FCSTD DOCUMENT  (FreeCAD 0.20R29410 (Git))
Label: Chamber0
License: All rights reserved
LicenseURL: http://en.wikipedia.org/wiki/All_rights_reserved
objects: Sketcher::SketchObject×3, PartDesign::Body×1
note: 4 computed .brp shape members not serialized (recipe doc carries the construction recipe); baked Part::Feature solids carry a one-line shape summary decoded from their .brp

FEATURE [PartDesign::Body] Body
  Origin = -> Origin
FEATURE [Sketcher::SketchObject] Sketch001
  FullyConstrained = false
  sketch-geometry (28):
    g0: ArcOfCircle CenterX=0 CenterY=0 CenterZ=0 NormalX=0 NormalY=0 NormalZ=1 AngleXU=0 Radius=100 StartAngle=0.785398 EndAngle=2.35619
    g1: Circle CenterX=0 CenterY=116 CenterZ=0 NormalX=0 NormalY=0 NormalZ=1 AngleXU=0 Radius=6
    g2: ArcOfCircle CenterX=0 CenterY=0 CenterZ=0 NormalX=0 NormalY=0 NormalZ=1 AngleXU=0 Radius=120 StartAngle=1.73306 EndAngle=2.35619
    g3: GeomPoint X=0 Y=100 Z=0
    g4: GeomPoint X=0 Y=120 Z=0
    g5: ArcOfCircle CenterX=0 CenterY=116 CenterZ=0 NormalX=0 NormalY=0 NormalZ=1 AngleXU=0 Radius=16 StartAngle=4.71239 EndAngle=4.71239
    g6: GeomPoint X=0 Y=132 Z=0
    g7: ArcOfCircle CenterX=0 CenterY=116 CenterZ=0 NormalX=0 NormalY=0 NormalZ=1 AngleXU=0 Radius=16 StartAngle=0.329187 EndAngle=2.75254
    g8: ArcOfCircle CenterX=-20.3559 CenterY=124.345 CenterZ=0 NormalX=0 NormalY=0 NormalZ=1 AngleXU=0 Radius=6 StartAngle=4.87466 EndAngle=5.89413
    g9: ArcOfCircle CenterX=0 CenterY=116 CenterZ=0 NormalX=0 NormalY=0 NormalZ=1 AngleXU=0 Radius=16 StartAngle=0.329187 EndAngle=2.75254
    g10: ArcOfCircle CenterX=18.7837 CenterY=122.417 CenterZ=0 NormalX=0 NormalY=0 NormalZ=1 AngleXU=0 Radius=3.84956 StartAngle=3.47078 EndAngle=4.56014
    g11: ArcOfCircle CenterX=0 CenterY=0 CenterZ=0 NormalX=0 NormalY=0 NormalZ=1 AngleXU=0 Radius=120 StartAngle=0.785398 EndAngle=1.41854
    g12: ArcOfCircle CenterX=0 CenterY=116 CenterZ=0 NormalX=0 NormalY=0 NormalZ=1 AngleXU=0 Radius=16 StartAngle=4.71239 EndAngle=4.71239
    g13: ArcOfCircle CenterX=0 CenterY=116 CenterZ=0 NormalX=0 NormalY=0 NormalZ=1 AngleXU=0 Radius=16 StartAngle=0.329187 EndAngle=2.75254
    g14: ArcOfCircle CenterX=0 CenterY=0 CenterZ=0 NormalX=0 NormalY=0 NormalZ=1 AngleXU=0 Radius=100 StartAngle=3.92699 EndAngle=5.49779
    g15: Circle CenterX=0 CenterY=-116 CenterZ=0 NormalX=0 NormalY=0 NormalZ=1 AngleXU=0 Radius=6
    g16: ArcOfCircle CenterX=0 CenterY=0 CenterZ=0 NormalX=0 NormalY=0 NormalZ=1 AngleXU=0 Radius=120 StartAngle=3.92699 EndAngle=4.55012
    g17: GeomPoint X=0 Y=-100 Z=0
    g18: GeomPoint X=0 Y=-120 Z=0
    g19: ArcOfCircle CenterX=0 CenterY=-116 CenterZ=0 NormalX=0 NormalY=0 NormalZ=1 AngleXU=0 Radius=16 StartAngle=1.5708 EndAngle=1.5708
    g20: GeomPoint X=0 Y=-132 Z=0
    g21: ArcOfCircle CenterX=0 CenterY=-116 CenterZ=0 NormalX=0 NormalY=0 NormalZ=1 AngleXU=0 Radius=16 StartAngle=3.53064 EndAngle=5.954
    g22: ArcOfCircle CenterX=-20.3559 CenterY=-124.345 CenterZ=0 NormalX=0 NormalY=0 NormalZ=1 AngleXU=0 Radius=6 StartAngle=0.389051 EndAngle=1.40853
    g23: ArcOfCircle CenterX=0 CenterY=-116 CenterZ=0 NormalX=0 NormalY=0 NormalZ=1 AngleXU=0 Radius=16 StartAngle=3.53064 EndAngle=5.954
    g24: ArcOfCircle CenterX=18.7837 CenterY=-122.417 CenterZ=0 NormalX=0 NormalY=0 NormalZ=1 AngleXU=0 Radius=3.84956 StartAngle=1.72305 EndAngle=2.81241
    g25: ArcOfCircle CenterX=0 CenterY=0 CenterZ=0 NormalX=0 NormalY=0 NormalZ=1 AngleXU=0 Radius=120 StartAngle=4.86464 EndAngle=5.49779
    g26: ArcOfCircle CenterX=0 CenterY=-116 CenterZ=0 NormalX=0 NormalY=0 NormalZ=1 AngleXU=0 Radius=16 StartAngle=1.5708 EndAngle=1.5708
    g27: ArcOfCircle CenterX=0 CenterY=-116 CenterZ=0 NormalX=0 NormalY=0 NormalZ=1 AngleXU=0 Radius=16 StartAngle=3.53064 EndAngle=5.954
  constraints (71):
    c: Coincident(g0,g-1)
    c: Radius(g0) = 100
    c: Radius(g1) = 6  'Main Screw Radius 0'
    c: Vertical(g1,g0)
    c: Coincident(g2,g0)
    c: PointOnObject(g3,g0)
    c: Vertical(g3,g0)
    c: PointOnObject(g4,g2)
    c: Vertical(g0,g4)
    c: Distance(g4,g3) = 20
    c: Coincident(g5,g1)
    c: Radius(g5) = 16  'Main Clamp Outer'
    c: PointOnObject(g6,g5)
    c: Vertical(g6,g1)
    c: Distance(g1,g3) = 16
    c: PointOnObject(g5,g0)
    c: Equal(g5,g7)
    c: Coincident(g5,g7)
    c: Tangent(g2,g8) = 1.5708
    c: Tangent(g7,g8) = 1.5708
    c: Radius(g8) = 6
    c: PointOnObject(g9,g8)
    c: Equal(g5,g9)
    c: PointOnObject(g12,g0)
    c: Coincident(g5,g9)
    c: Tangent(g7,g10) = 1.5708
    c: Coincident(g11,g10) = 1.5708
    c: PointOnObject(g9,g10)
    c: Equal(g2,g11)
    c: Coincident(g2,g11)
    c: Equal(g5,g12)
    c: PointOnObject(g13,g8)
    c: PointOnObject(g12,g0)
    c: Coincident(g5,g12)
    c: Equal(g5,g13)
    c: PointOnObject(g5,g0)
    c: PointOnObject(g13,g10)
    c: Coincident(g5,g13)
    c: Radius(g14) = 100
    c: Radius(g15) = 6  'Main Screw Radius 0'
    c: Coincident(g16,g14)
    c: PointOnObject(g17,g14)
    c: PointOnObject(g18,g16)
    c: Distance(g18,g17) = 20
    c: Coincident(g19,g15)
    c: Radius(g19) = 16  'Main Clamp Outer'
    c: PointOnObject(g20,g19)
    c: Distance(g15,g17) = 16
    c: PointOnObject(g19,g14)
    c: Equal(g19,g21)
    c: Coincident(g19,g21)
    c: Tangent(g16,g22) = 1.5708
    c: Tangent(g21,g22) = 1.5708
    c: Radius(g22) = 6
    c: PointOnObject(g23,g22)
    c: Equal(g19,g23)
    c: PointOnObject(g26,g14)
    c: Coincident(g19,g23)
    c: Tangent(g21,g24) = 1.5708
    c: Coincident(g25,g24) = 1.5708
    c: PointOnObject(g23,g24)
    c: Equal(g16,g25)
    c: Coincident(g16,g25)
    c: Equal(g19,g26)
    c: PointOnObject(g27,g22)
    c: PointOnObject(g26,g14)
    c: Coincident(g19,g26)
    c: Equal(g19,g27)
    c: PointOnObject(g19,g14)
    c: PointOnObject(g27,g24)
    c: Coincident(g19,g27)
FEATURE [Sketcher::SketchObject] Sketch002
  FullyConstrained = false
  Placement = pos=(0,0,0) rot=(0,0,1;1.5708rad)
  sketch-geometry (28):
    g0: ArcOfCircle CenterX=0 CenterY=0 CenterZ=0 NormalX=0 NormalY=0 NormalZ=1 AngleXU=0 Radius=100 StartAngle=0.785398 EndAngle=2.35619
    g1: Circle CenterX=0 CenterY=116 CenterZ=0 NormalX=0 NormalY=0 NormalZ=1 AngleXU=0 Radius=6
    g2: ArcOfCircle CenterX=0 CenterY=0 CenterZ=0 NormalX=0 NormalY=0 NormalZ=1 AngleXU=0 Radius=120 StartAngle=1.73306 EndAngle=2.35619
    g3: GeomPoint X=0 Y=100 Z=0
    g4: GeomPoint X=0 Y=120 Z=0
    g5: ArcOfCircle CenterX=0 CenterY=116 CenterZ=0 NormalX=0 NormalY=0 NormalZ=1 AngleXU=0 Radius=16 StartAngle=4.71239 EndAngle=4.71239
    g6: GeomPoint X=0 Y=132 Z=0
    g7: ArcOfCircle CenterX=0 CenterY=116 CenterZ=0 NormalX=0 NormalY=0 NormalZ=1 AngleXU=0 Radius=16 StartAngle=0.329187 EndAngle=2.75254
    g8: ArcOfCircle CenterX=-20.3559 CenterY=124.345 CenterZ=0 NormalX=0 NormalY=0 NormalZ=1 AngleXU=0 Radius=6 StartAngle=4.87466 EndAngle=5.89413
    g9: ArcOfCircle CenterX=0 CenterY=116 CenterZ=0 NormalX=0 NormalY=0 NormalZ=1 AngleXU=0 Radius=16 StartAngle=0.329187 EndAngle=2.75254
    g10: ArcOfCircle CenterX=18.7837 CenterY=122.417 CenterZ=0 NormalX=0 NormalY=0 NormalZ=1 AngleXU=0 Radius=3.84956 StartAngle=3.47078 EndAngle=4.56014
    g11: ArcOfCircle CenterX=0 CenterY=0 CenterZ=0 NormalX=0 NormalY=0 NormalZ=1 AngleXU=0 Radius=120 StartAngle=0.785398 EndAngle=1.41854
    g12: ArcOfCircle CenterX=0 CenterY=116 CenterZ=0 NormalX=0 NormalY=0 NormalZ=1 AngleXU=0 Radius=16 StartAngle=4.71239 EndAngle=4.71239
    g13: ArcOfCircle CenterX=0 CenterY=116 CenterZ=0 NormalX=0 NormalY=0 NormalZ=1 AngleXU=0 Radius=16 StartAngle=0.329187 EndAngle=2.75254
    g14: ArcOfCircle CenterX=0 CenterY=0 CenterZ=0 NormalX=0 NormalY=0 NormalZ=1 AngleXU=0 Radius=100 StartAngle=3.92699 EndAngle=5.49779
    g15: Circle CenterX=0 CenterY=-116 CenterZ=0 NormalX=0 NormalY=0 NormalZ=1 AngleXU=0 Radius=6
    g16: ArcOfCircle CenterX=0 CenterY=0 CenterZ=0 NormalX=0 NormalY=0 NormalZ=1 AngleXU=0 Radius=120 StartAngle=3.92699 EndAngle=4.55012
    g17: GeomPoint X=0 Y=-100 Z=0
    g18: GeomPoint X=0 Y=-120 Z=0
    g19: ArcOfCircle CenterX=0 CenterY=-116 CenterZ=0 NormalX=0 NormalY=0 NormalZ=1 AngleXU=0 Radius=16 StartAngle=1.5708 EndAngle=1.5708
    g20: GeomPoint X=0 Y=-132 Z=0
    g21: ArcOfCircle CenterX=0 CenterY=-116 CenterZ=0 NormalX=0 NormalY=0 NormalZ=1 AngleXU=0 Radius=16 StartAngle=3.53064 EndAngle=5.954
    g22: ArcOfCircle CenterX=-20.3559 CenterY=-124.345 CenterZ=0 NormalX=0 NormalY=0 NormalZ=1 AngleXU=0 Radius=6 StartAngle=0.389051 EndAngle=1.40853
    g23: ArcOfCircle CenterX=0 CenterY=-116 CenterZ=0 NormalX=0 NormalY=0 NormalZ=1 AngleXU=0 Radius=16 StartAngle=3.53064 EndAngle=5.954
    g24: ArcOfCircle CenterX=18.7837 CenterY=-122.417 CenterZ=0 NormalX=0 NormalY=0 NormalZ=1 AngleXU=0 Radius=3.84956 StartAngle=1.72305 EndAngle=2.81241
    g25: ArcOfCircle CenterX=0 CenterY=0 CenterZ=0 NormalX=0 NormalY=0 NormalZ=1 AngleXU=0 Radius=120 StartAngle=4.86464 EndAngle=5.49779
    g26: ArcOfCircle CenterX=0 CenterY=-116 CenterZ=0 NormalX=0 NormalY=0 NormalZ=1 AngleXU=0 Radius=16 StartAngle=1.5708 EndAngle=1.5708
    g27: ArcOfCircle CenterX=0 CenterY=-116 CenterZ=0 NormalX=0 NormalY=0 NormalZ=1 AngleXU=0 Radius=16 StartAngle=3.53064 EndAngle=5.954
  constraints (71):
    c: Coincident(g0,g-1)
    c: Radius(g0) = 100
    c: Radius(g1) = 6  'Main Screw Radius 0'
    c: Vertical(g1,g0)
    c: Coincident(g2,g0)
    c: PointOnObject(g3,g0)
    c: Vertical(g3,g0)
    c: PointOnObject(g4,g2)
    c: Vertical(g0,g4)
    c: Distance(g4,g3) = 20
    c: Coincident(g5,g1)
    c: Radius(g5) = 16  'Main Clamp Outer'
    c: PointOnObject(g6,g5)
    c: Vertical(g6,g1)
    c: Distance(g1,g3) = 16
    c: PointOnObject(g5,g0)
    c: Equal(g5,g7)
    c: Coincident(g5,g7)
    c: Tangent(g2,g8) = 1.5708
    c: Tangent(g7,g8) = 1.5708
    c: Radius(g8) = 6
    c: PointOnObject(g9,g8)
    c: Equal(g5,g9)
    c: PointOnObject(g12,g0)
    c: Coincident(g5,g9)
    c: Tangent(g7,g10) = 1.5708
    c: Coincident(g11,g10) = 1.5708
    c: PointOnObject(g9,g10)
    c: Equal(g2,g11)
    c: Coincident(g2,g11)
    c: Equal(g5,g12)
    c: PointOnObject(g13,g8)
    c: PointOnObject(g12,g0)
    c: Coincident(g5,g12)
    c: Equal(g5,g13)
    c: PointOnObject(g5,g0)
    c: PointOnObject(g13,g10)
    c: Coincident(g5,g13)
    c: Radius(g14) = 100
    c: Radius(g15) = 6  'Main Screw Radius 0'
    c: Coincident(g16,g14)
    c: PointOnObject(g17,g14)
    c: PointOnObject(g18,g16)
    c: Distance(g18,g17) = 20
    c: Coincident(g19,g15)
    c: Radius(g19) = 16  'Main Clamp Outer'
    c: PointOnObject(g20,g19)
    c: Distance(g15,g17) = 16
    c: PointOnObject(g19,g14)
    c: Equal(g19,g21)
    c: Coincident(g19,g21)
    c: Tangent(g16,g22) = 1.5708
    c: Tangent(g21,g22) = 1.5708
    c: Radius(g22) = 6
    c: PointOnObject(g23,g22)
    c: Equal(g19,g23)
    c: PointOnObject(g26,g14)
    c: Coincident(g19,g23)
    c: Tangent(g21,g24) = 1.5708
    c: Coincident(g25,g24) = 1.5708
    c: PointOnObject(g23,g24)
    c: Equal(g16,g25)
    c: Coincident(g16,g25)
    c: Equal(g19,g26)
    c: PointOnObject(g27,g22)
    c: PointOnObject(g26,g14)
    c: Coincident(g19,g26)
    c: Equal(g19,g27)
    c: PointOnObject(g19,g14)
    c: PointOnObject(g27,g24)
    c: Coincident(g19,g27)
FEATURE [Sketcher::SketchObject] Sketch
  FullyConstrained = false
  Placement = pos=(0,0,0) rot=(0,0,1;1.5708rad)
  sketch-geometry (56):
    g0: ArcOfCircle CenterX=0 CenterY=0 CenterZ=0 NormalX=0 NormalY=0 NormalZ=1 AngleXU=0 Radius=100 StartAngle=0.785398 EndAngle=2.35619
    g1: Circle CenterX=0 CenterY=116 CenterZ=0 NormalX=0 NormalY=0 NormalZ=1 AngleXU=0 Radius=6
    g2: ArcOfCircle CenterX=0 CenterY=0 CenterZ=0 NormalX=0 NormalY=0 NormalZ=1 AngleXU=0 Radius=120 StartAngle=1.73306 EndAngle=2.35619
    g3: GeomPoint X=0 Y=100 Z=0
    g4: GeomPoint X=0 Y=120 Z=0
    g5: ArcOfCircle CenterX=0 CenterY=116 CenterZ=0 NormalX=0 NormalY=0 NormalZ=1 AngleXU=0 Radius=16 StartAngle=4.71239 EndAngle=4.71239
    g6: GeomPoint X=0 Y=132 Z=0
    g7: ArcOfCircle CenterX=0 CenterY=116 CenterZ=0 NormalX=0 NormalY=0 NormalZ=1 AngleXU=0 Radius=16 StartAngle=0.329187 EndAngle=2.75254
    g8: ArcOfCircle CenterX=-20.3559 CenterY=124.345 CenterZ=0 NormalX=0 NormalY=0 NormalZ=1 AngleXU=0 Radius=6 StartAngle=4.87466 EndAngle=5.89413
    g9: ArcOfCircle CenterX=0 CenterY=116 CenterZ=0 NormalX=0 NormalY=0 NormalZ=1 AngleXU=0 Radius=16 StartAngle=0.329187 EndAngle=2.75254
    g10: ArcOfCircle CenterX=18.7837 CenterY=122.417 CenterZ=0 NormalX=0 NormalY=0 NormalZ=1 AngleXU=0 Radius=3.84956 StartAngle=3.47078 EndAngle=4.56014
    g11: ArcOfCircle CenterX=0 CenterY=0 CenterZ=0 NormalX=0 NormalY=0 NormalZ=1 AngleXU=0 Radius=120 StartAngle=0.785398 EndAngle=1.41854
    g12: ArcOfCircle CenterX=0 CenterY=116 CenterZ=0 NormalX=0 NormalY=0 NormalZ=1 AngleXU=0 Radius=16 StartAngle=4.71239 EndAngle=4.71239
    g13: ArcOfCircle CenterX=0 CenterY=116 CenterZ=0 NormalX=0 NormalY=0 NormalZ=1 AngleXU=0 Radius=16 StartAngle=0.329187 EndAngle=2.75254
    g14: ArcOfCircle CenterX=0 CenterY=0 CenterZ=0 NormalX=0 NormalY=0 NormalZ=1 AngleXU=0 Radius=100 StartAngle=3.92699 EndAngle=5.49779
    g15: Circle CenterX=0 CenterY=-116 CenterZ=0 NormalX=0 NormalY=0 NormalZ=1 AngleXU=0 Radius=6
    g16: ArcOfCircle CenterX=0 CenterY=0 CenterZ=0 NormalX=0 NormalY=0 NormalZ=1 AngleXU=0 Radius=120 StartAngle=3.92699 EndAngle=4.55012
    g17: GeomPoint X=0 Y=-100 Z=0
    g18: GeomPoint X=0 Y=-120 Z=0
    g19: ArcOfCircle CenterX=0 CenterY=-116 CenterZ=0 NormalX=0 NormalY=0 NormalZ=1 AngleXU=0 Radius=16 StartAngle=1.5708 EndAngle=1.5708
    g20: GeomPoint X=0 Y=-132 Z=0
    g21: ArcOfCircle CenterX=0 CenterY=-116 CenterZ=0 NormalX=0 NormalY=0 NormalZ=1 AngleXU=0 Radius=16 StartAngle=3.53064 EndAngle=5.954
    g22: ArcOfCircle CenterX=-20.3559 CenterY=-124.345 CenterZ=0 NormalX=0 NormalY=0 NormalZ=1 AngleXU=0 Radius=6 StartAngle=0.389051 EndAngle=1.40853
    g23: ArcOfCircle CenterX=0 CenterY=-116 CenterZ=0 NormalX=0 NormalY=0 NormalZ=1 AngleXU=0 Radius=16 StartAngle=3.53064 EndAngle=5.954
    g24: ArcOfCircle CenterX=18.7837 CenterY=-122.417 CenterZ=0 NormalX=0 NormalY=0 NormalZ=1 AngleXU=0 Radius=3.84956 StartAngle=1.72305 EndAngle=2.81241
    g25: ArcOfCircle CenterX=0 CenterY=0 CenterZ=0 NormalX=0 NormalY=0 NormalZ=1 AngleXU=0 Radius=120 StartAngle=4.86464 EndAngle=5.49779
    g26: ArcOfCircle CenterX=0 CenterY=-116 CenterZ=0 NormalX=0 NormalY=0 NormalZ=1 AngleXU=0 Radius=16 StartAngle=1.5708 EndAngle=1.5708
    g27: ArcOfCircle CenterX=0 CenterY=-116 CenterZ=0 NormalX=0 NormalY=0 NormalZ=1 AngleXU=0 Radius=16 StartAngle=3.53064 EndAngle=5.954
    g28: ArcOfCircle CenterX=0 CenterY=0 CenterZ=0 NormalX=0 NormalY=0 NormalZ=1 AngleXU=0 Radius=100 StartAngle=0.785398 EndAngle=2.35619
    g29: Circle CenterX=0 CenterY=116 CenterZ=0 NormalX=0 NormalY=0 NormalZ=1 AngleXU=0 Radius=6
    g30: ArcOfCircle CenterX=0 CenterY=0 CenterZ=0 NormalX=0 NormalY=0 NormalZ=1 AngleXU=0 Radius=120 StartAngle=1.73306 EndAngle=2.35619
    g31: GeomPoint X=0 Y=100 Z=0
    g32: GeomPoint X=0 Y=120 Z=0
    g33: ArcOfCircle CenterX=0 CenterY=116 CenterZ=0 NormalX=0 NormalY=0 NormalZ=1 AngleXU=0 Radius=16 StartAngle=4.71239 EndAngle=4.71239
    g34: GeomPoint X=0 Y=132 Z=0
    g35: ArcOfCircle CenterX=0 CenterY=116 CenterZ=0 NormalX=0 NormalY=0 NormalZ=1 AngleXU=0 Radius=16 StartAngle=0.329187 EndAngle=2.75254
    g36: ArcOfCircle CenterX=-20.3559 CenterY=124.345 CenterZ=0 NormalX=0 NormalY=0 NormalZ=1 AngleXU=0 Radius=6 StartAngle=4.87466 EndAngle=5.89413
    g37: ArcOfCircle CenterX=0 CenterY=116 CenterZ=0 NormalX=0 NormalY=0 NormalZ=1 AngleXU=0 Radius=16 StartAngle=0.329187 EndAngle=2.75254
    g38: ArcOfCircle CenterX=18.7837 CenterY=122.417 CenterZ=0 NormalX=0 NormalY=0 NormalZ=1 AngleXU=0 Radius=3.84956 StartAngle=3.47078 EndAngle=4.56014
    g39: ArcOfCircle CenterX=0 CenterY=0 CenterZ=0 NormalX=0 NormalY=0 NormalZ=1 AngleXU=0 Radius=120 StartAngle=0.785398 EndAngle=1.41854
    g40: ArcOfCircle CenterX=0 CenterY=116 CenterZ=0 NormalX=0 NormalY=0 NormalZ=1 AngleXU=0 Radius=16 StartAngle=4.71239 EndAngle=4.71239
    g41: ArcOfCircle CenterX=0 CenterY=116 CenterZ=0 NormalX=0 NormalY=0 NormalZ=1 AngleXU=0 Radius=16 StartAngle=0.329187 EndAngle=2.75254
    g42: ArcOfCircle CenterX=0 CenterY=0 CenterZ=0 NormalX=0 NormalY=0 NormalZ=1 AngleXU=0 Radius=100 StartAngle=3.92699 EndAngle=5.49779
    g43: Circle CenterX=0 CenterY=-116 CenterZ=0 NormalX=0 NormalY=0 NormalZ=1 AngleXU=0 Radius=6
    g44: ArcOfCircle CenterX=0 CenterY=0 CenterZ=0 NormalX=0 NormalY=0 NormalZ=1 AngleXU=0 Radius=120 StartAngle=3.92699 EndAngle=4.55012
    g45: GeomPoint X=0 Y=-100 Z=0
    g46: GeomPoint X=0 Y=-120 Z=0
    g47: ArcOfCircle CenterX=0 CenterY=-116 CenterZ=0 NormalX=0 NormalY=0 NormalZ=1 AngleXU=0 Radius=16 StartAngle=1.5708 EndAngle=1.5708
    g48: GeomPoint X=0 Y=-132 Z=0
    g49: ArcOfCircle CenterX=0 CenterY=-116 CenterZ=0 NormalX=0 NormalY=0 NormalZ=1 AngleXU=0 Radius=16 StartAngle=3.53064 EndAngle=5.954
    g50: ArcOfCircle CenterX=-20.3559 CenterY=-124.345 CenterZ=0 NormalX=0 NormalY=0 NormalZ=1 AngleXU=0 Radius=6 StartAngle=0.389051 EndAngle=1.40853
    g51: ArcOfCircle CenterX=0 CenterY=-116 CenterZ=0 NormalX=0 NormalY=0 NormalZ=1 AngleXU=0 Radius=16 StartAngle=3.53064 EndAngle=5.954
    g52: ArcOfCircle CenterX=18.7837 CenterY=-122.417 CenterZ=0 NormalX=0 NormalY=0 NormalZ=1 AngleXU=0 Radius=3.84956 StartAngle=1.72305 EndAngle=2.81241
    g53: ArcOfCircle CenterX=0 CenterY=0 CenterZ=0 NormalX=0 NormalY=0 NormalZ=1 AngleXU=0 Radius=120 StartAngle=4.86464 EndAngle=5.49779
    g54: ArcOfCircle CenterX=0 CenterY=-116 CenterZ=0 NormalX=0 NormalY=0 NormalZ=1 AngleXU=0 Radius=16 StartAngle=1.5708 EndAngle=1.5708
    g55: ArcOfCircle CenterX=0 CenterY=-116 CenterZ=0 NormalX=0 NormalY=0 NormalZ=1 AngleXU=0 Radius=16 StartAngle=3.53064 EndAngle=5.954
  constraints (142):
    c: Coincident(g0,g-1)
    c: Radius(g0) = 100
    c: Radius(g1) = 6  'Main Screw Radius 0'
    c: Vertical(g1,g0)
    c: Coincident(g2,g0)
    c: PointOnObject(g3,g0)
    c: Vertical(g3,g0)
    c: PointOnObject(g4,g2)
    c: Vertical(g0,g4)
    c: Distance(g4,g3) = 20
    c: Coincident(g5,g1)
    c: Radius(g5) = 16  'Main Clamp Outer'
    c: PointOnObject(g6,g5)
    c: Vertical(g6,g1)
    c: Distance(g1,g3) = 16
    c: PointOnObject(g5,g0)
    c: Equal(g5,g7)
    c: Coincident(g5,g7)
    c: Tangent(g2,g8) = 1.5708
    c: Tangent(g7,g8) = 1.5708
    c: Radius(g8) = 6
    c: PointOnObject(g9,g8)
    c: Equal(g5,g9)
    c: PointOnObject(g12,g0)
    c: Coincident(g5,g9)
    c: Tangent(g7,g10) = 1.5708
    c: Coincident(g11,g10) = 1.5708
    c: PointOnObject(g9,g10)
    c: Equal(g2,g11)
    c: Coincident(g2,g11)
    c: Equal(g5,g12)
    c: PointOnObject(g13,g8)
    c: PointOnObject(g12,g0)
    c: Coincident(g5,g12)
    c: Equal(g5,g13)
    c: PointOnObject(g5,g0)
    c: PointOnObject(g13,g10)
    c: Coincident(g5,g13)
    c: Radius(g14) = 100
    c: Radius(g15) = 6  'Main Screw Radius 0'
    c: Coincident(g16,g14)
    c: PointOnObject(g17,g14)
    c: PointOnObject(g18,g16)
    c: Distance(g18,g17) = 20
    c: Coincident(g19,g15)
    c: Radius(g19) = 16  'Main Clamp Outer'
    c: PointOnObject(g20,g19)
    c: Distance(g15,g17) = 16
    c: PointOnObject(g19,g14)
    c: Equal(g19,g21)
    c: Coincident(g19,g21)
    c: Tangent(g16,g22) = 1.5708
    c: Tangent(g21,g22) = 1.5708
    c: Radius(g22) = 6
    c: PointOnObject(g23,g22)
    c: Equal(g19,g23)
    c: PointOnObject(g26,g14)
    c: Coincident(g19,g23)
    c: Tangent(g21,g24) = 1.5708
    c: Coincident(g25,g24) = 1.5708
    c: PointOnObject(g23,g24)
    c: Equal(g16,g25)
    c: Coincident(g16,g25)
    c: Equal(g19,g26)
    c: PointOnObject(g27,g22)
    c: PointOnObject(g26,g14)
    c: Coincident(g19,g26)
    c: Equal(g19,g27)
    c: PointOnObject(g19,g14)
    c: PointOnObject(g27,g24)
    c: Coincident(g19,g27)
    c: Coincident(g28,g-1)
    c: Radius(g28) = 100
    c: Radius(g29) = 6  'Main Screw Radius 0'
    c: Vertical(g29,g28)
    c: Coincident(g30,g28)
    c: PointOnObject(g31,g28)
    c: Vertical(g31,g28)
    c: PointOnObject(g32,g30)
    c: Vertical(g28,g32)
    c: Distance(g32,g31) = 20
    c: Coincident(g33,g29)
    c: Radius(g33) = 16  'Main Clamp Outer'
    c: PointOnObject(g34,g33)
    c: Vertical(g34,g29)
    c: Distance(g29,g31) = 16
    c: PointOnObject(g33,g28)
    c: Equal(g33,g35)
    c: Coincident(g33,g35)
    c: Tangent(g30,g36) = 1.5708
    c: Tangent(g35,g36) = 1.5708
    c: Radius(g36) = 6
    c: PointOnObject(g37,g36)
    c: Equal(g33,g37)
    c: PointOnObject(g40,g28)
    c: Coincident(g33,g37)
    c: Tangent(g35,g38) = 1.5708
    c: Coincident(g39,g38) = 1.5708
    c: PointOnObject(g37,g38)
    c: Equal(g30,g39)
    c: Coincident(g30,g39)
    c: Equal(g33,g40)
    c: PointOnObject(g41,g36)
    c: PointOnObject(g40,g28)
    c: Coincident(g33,g40)
    c: Equal(g33,g41)
    c: PointOnObject(g33,g28)
    c: PointOnObject(g41,g38)
    c: Coincident(g33,g41)
    c: Radius(g42) = 100
    c: Radius(g43) = 6  'Main Screw Radius 0'
    c: Coincident(g44,g42)
    c: PointOnObject(g45,g42)
    c: PointOnObject(g46,g44)
    c: Distance(g46,g45) = 20
    c: Coincident(g47,g43)
    c: Radius(g47) = 16  'Main Clamp Outer'
    c: PointOnObject(g48,g47)
    c: Distance(g43,g45) = 16
    c: PointOnObject(g47,g42)
    c: Equal(g47,g49)
    c: Coincident(g47,g49)
    c: Tangent(g44,g50) = 1.5708
    c: Tangent(g49,g50) = 1.5708
    c: Radius(g50) = 6
    c: PointOnObject(g51,g50)
    c: Equal(g47,g51)
    c: PointOnObject(g54,g42)
    c: Coincident(g47,g51)
    c: Tangent(g49,g52) = 1.5708
    c: Coincident(g53,g52) = 1.5708
    c: PointOnObject(g51,g52)
    c: Equal(g44,g53)
    c: Coincident(g44,g53)
    c: Equal(g47,g54)
    c: PointOnObject(g55,g50)
    c: PointOnObject(g54,g42)
    c: Coincident(g47,g54)
    c: Equal(g47,g55)
    c: PointOnObject(g47,g42)
    c: PointOnObject(g55,g52)
    c: Coincident(g47,g55)
